MODEL slx_2b29faa2a7fa
CONFIG AbsTol = 1e-3
CONFIG EnableMultiTasking = off
CONFIG FixedStep = auto
CONFIG MaxStep = auto
CONFIG MinStep = auto
CONFIG RelTol = 1e-3
CONFIG SampleTimeConstraint = Unconstrained
CONFIG SolverName = VariableStepAuto
CONFIG StartTime = 0.0
CONFIG StopTime = 2
BLOCK [Reference] Ideal Force Source  REF=fl_lib/Mechanical/Mechanical Sources/Ideal Force Source
  Ports = [0, 0, 0, 0, 0, 1, 2]
  SourceBlock = fl_lib/Mechanical/Mechanical Sources/Ideal Force Source
  SourceProductBaseCode = SS
  SourceType = Ideal Force Source
BLOCK [Reference] Ideal Translational Motion Sensor  REF=fl_lib/Mechanical/Mechanical Sensors/Ideal Translational
Motion Sensor
  Ports = [0, 0, 0, 0, 0, 1, 3]
  SourceBlock = fl_lib/Mechanical/Mechanical Sensors/Ideal Translational
Motion Sensor
  SourceProductBaseCode = SS
  SourceType = Ideal Translational
Motion Sensor
BLOCK [Reference] Mass  REF=fl_lib/Mechanical/Translational
Elements/Mass
  NameLocation = top
  Ports = [0, 0, 0, 0, 0, 1]
  SourceBlock = fl_lib/Mechanical/Translational
Elements/Mass
  SourceProductBaseCode = SS
  SourceType = Mass
BLOCK [Reference] Mechanical Translational Reference  REF=fl_lib/Mechanical/Translational
Elements/Mechanical
Translational
Reference
  Ports = [0, 0, 0, 0, 0, 1]
  SourceBlock = fl_lib/Mechanical/Translational
Elements/Mechanical
Translational
Reference
  SourceProductName = Foundation Library
  SourceType = Mechanical
Translational
Reference
BLOCK [Reference] PS-Simulink Converter  REF=nesl_utility/PS-Simulink
Converter
  Ports = [0, 1, 0, 0, 0, 1]
  SourceBlock = nesl_utility/PS-Simulink
Converter
  SourceProductName = Utilities
  SourceType = PS-Simulink
Converter
BLOCK [Scope] Scope
  Floating = off
  NumInputPorts = 1
  Ports = [1]
  ScopeSpecificationString = Simulink.scopes.TimeScopeBlockCfg('CurrentConfiguration', extmgr.ConfigurationSet(extmgr.Configuration('Core','General UI',true),extmgr.Configuration('Core','Source UI',true),extmgr.Configuration('Sources','WiredSimulink',true),extmgr.Configuration('Visuals','Time Domain',true,'SerializedDisplays',{struct('MinYLimReal','-0.14319','MaxYLimReal','0.28275','YLabelReal','','MinYLimMag','0.00000','MaxY...<+1396ch>
BLOCK [Reference] Simulink-PS Converter  REF=nesl_utility/Simulink-PS
Converter
  Ports = [1, 0, 0, 0, 0, 0, 1]
  SourceBlock = nesl_utility/Simulink-PS
Converter
  SourceProductName = Utilities
  SourceType = Simulink-PS
Converter
BLOCK [Sin] Sine Wave
  Amplitude = A
  Frequency = omega
  Ports = [0, 1]
  SampleTime = 0
BLOCK [Reference] Solver Configuration  REF=nesl_utility/Solver
Configuration
  Ports = [0, 0, 0, 0, 0, 0, 1]
  SourceBlock = nesl_utility/Solver
Configuration
  SourceProductName = Utilities
  SourceType = Solver
Configuration
BLOCK [Reference] Translational Damper  REF=fl_lib/Mechanical/Translational
Elements/Translational Damper
  NameLocation = left
  Ports = [0, 0, 0, 0, 0, 1, 1]
  SourceBlock = fl_lib/Mechanical/Translational
Elements/Translational Damper
  SourceProductBaseCode = SS
  SourceType = Translational Damper
BLOCK [Reference] Translational Spring  REF=fl_lib/Mechanical/Translational
Elements/Translational Spring
  NameLocation = left
  Ports = [0, 0, 0, 0, 0, 1, 1]
  SourceBlock = fl_lib/Mechanical/Translational
Elements/Translational Spring
  SourceProductBaseCode = SS
  SourceType = Translational Spring
LINE Ideal Force Source:rconn -> Simulink-PS Converter:rconn
LINE Ideal Translational Motion Sensor:rconn -> PS-Simulink Converter:lconn
LINE PS-Simulink Converter:1 -> Scope:1
LINE Sine Wave:1 -> Simulink-PS Converter:1
LINE Solver Configuration:rconn -> Mechanical Translational Reference:lconn
LINE Translational Damper:lconn -> Mass:lconn
